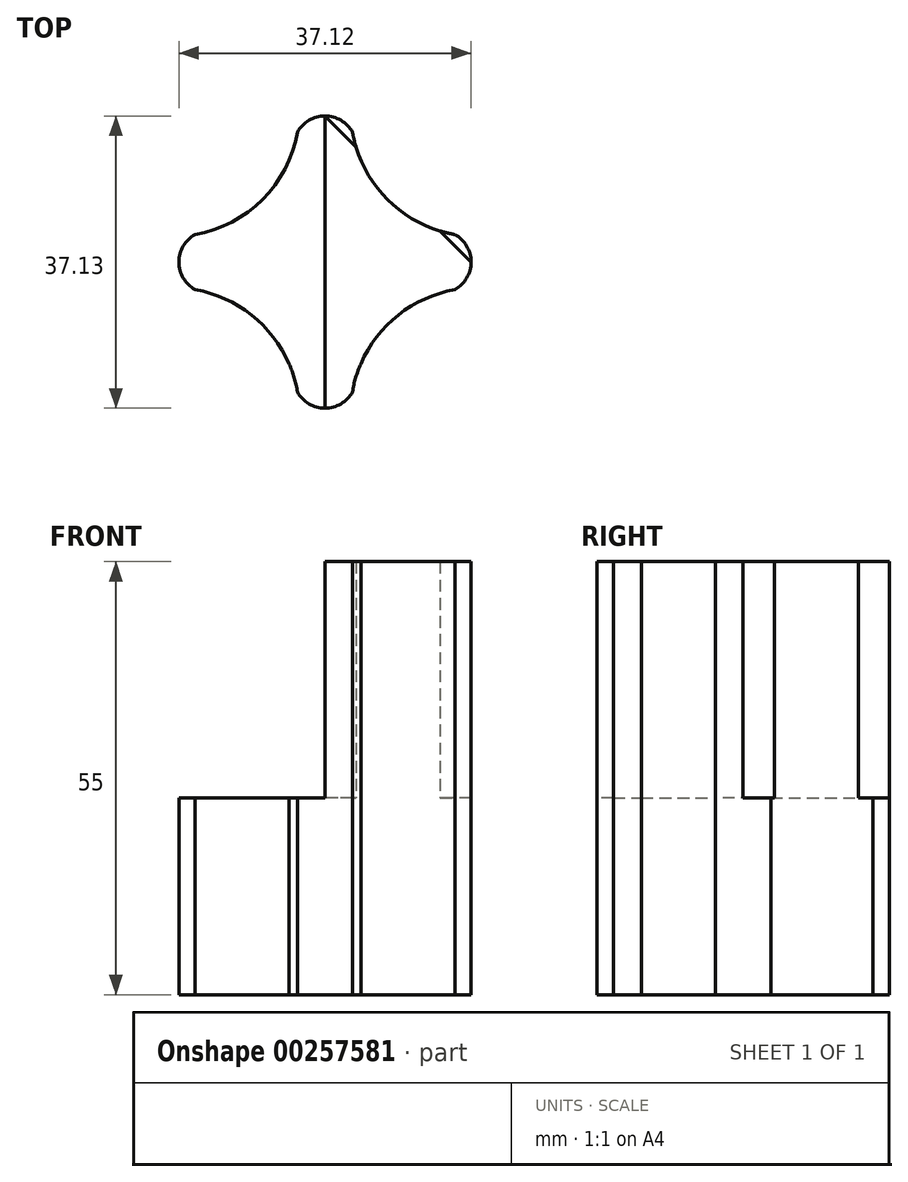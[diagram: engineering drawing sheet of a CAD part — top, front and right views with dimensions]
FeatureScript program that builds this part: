
annotation { "Feature Type Name" : "Feature", "Feature Type Description" : "" }
export const myFeature = defineFeature(function(context is Context, id is Id, definition is map)
    precondition{}
    {
        {
            var Q0;
            Q0=qCreatedBy(makeId("Top.planeOp"),FACE);
            var sketch = newSketch(context, id + "F0", { "sketchPlane" : qUnion([Q0])});
            skPoint(sketch, "E0", {"position": v(0.76, 10.62) * mm});
            skPoint(sketch, "E1", {"position": v(17.26, -5.88) * mm});
            skArc(sketch, "E2", {"start": v(4.26, 10.62) * mm, "mid": v(8.7, 2.06) * mm, "end": v(17.26, -2.38) * mm});
            skArc(sketch, "E3.MirrorCS", {"start": v(4.26, -22.38) * mm, "mid": v(8.7, -13.83) * mm, "end": v(17.26, -9.38) * mm});
            skArc(sketch, "E4.MirrorCS", {"start": v(-2.74, 10.62) * mm, "mid": v(-7.19, 2.06) * mm, "end": v(-15.74, -2.38) * mm});
            skArc(sketch, "E5.MirrorCS", {"start": v(-2.74, -22.38) * mm, "mid": v(-7.19, -13.83) * mm, "end": v(-15.74, -9.38) * mm});
            skArc(sketch, "E6", {"start": v(4.26, 10.62) * mm, "mid": v(0.76, 12.68) * mm, "end": v(-2.74, 10.62) * mm});
            skArc(sketch, "E7.MirrorCS", {"start": v(4.26, -22.38) * mm, "mid": v(0.76, -24.45) * mm, "end": v(-2.74, -22.38) * mm});
            skArc(sketch, "E8", {"start": v(17.26, -9.38) * mm, "mid": v(19.32, -5.88) * mm, "end": v(17.26, -2.38) * mm});
            skArc(sketch, "E9.MirrorCS", {"start": v(-15.74, -9.38) * mm, "mid": v(-17.8, -5.88) * mm, "end": v(-15.74, -2.38) * mm});
            skArc(sketch, "E10", {"start": v(-8.77, 16.95) * mm, "mid": v(0.83, 12.68) * mm, "end": v(10.38, 17.05) * mm});
            skArc(sketch, "E11.1.0", {"start": v(-20.21, -5.21) * mm, "mid": v(-13.18, 2.6) * mm, "end": v(-14.4, 13.04) * mm});
            skArc(sketch, "E11.2.0", {"start": v(-2.67, -22.94) * mm, "mid": v(-7.93, -13.84) * mm, "end": v(-18.23, -11.77) * mm});
            skArc(sketch, "E11.3.0", {"start": v(19.61, -11.74) * mm, "mid": v(9.34, -13.92) * mm, "end": v(4.18, -23.08) * mm});
            skArc(sketch, "E11.4.0", {"start": v(15.84, 12.92) * mm, "mid": v(14.75, 2.47) * mm, "end": v(21.86, -5.26) * mm});
            skPoint(sketch, "E11.center", {"position": v(0.76, -2) * mm});
            skArc(sketch, "E12", {"start": v(-2.67, -22.94) * mm, "mid": v(0.72, -24.94) * mm, "end": v(4.18, -23.08) * mm});
            skArc(sketch, "E13.1.0", {"start": v(-20.21, -5.21) * mm, "mid": v(-21.07, -9.05) * mm, "end": v(-18.23, -11.77) * mm});
            skArc(sketch, "E13.2.0", {"start": v(-8.77, 16.95) * mm, "mid": v(-12.69, 16.58) * mm, "end": v(-14.4, 13.04) * mm});
            skArc(sketch, "E13.3.0", {"start": v(15.84, 12.92) * mm, "mid": v(14.28, 16.53) * mm, "end": v(10.38, 17.05) * mm});
            skArc(sketch, "E13.4.0", {"start": v(19.61, -11.74) * mm, "mid": v(22.57, -9.14) * mm, "end": v(21.86, -5.26) * mm});
            skLineSegment(sketch, "E13.anchor1", {"start": v(0.76, -2) * mm, "end": v(-2.67, -22.94) * mm, "construction": true});
            skLineSegment(sketch, "E13.anchor2", {"start": v(0.76, -2) * mm, "end": v(19.61, -11.74) * mm, "construction": true});
            skSolve(sketch);
        }
        {
            var Q0;
            {var subQ9=sQuery(id+"F0.wireOp",EDGE,"E2");Q0=makeQuery(id+"F0.imprint","IMPRINT",FACE,{"disambiguationData":[TD([[makeQuery(id+"F0.imprint","IMPRINT",EDGE,{"derivedFrom":subQ9}),-1.0]])]});}
            extrude(context, id + "F1", {"entities" : qUnion([Q0]), "depth" : 25 * mm});
        }
        {
            var Q0;
            Q0=makeQuery(id+"F1.opExtrude","CAP_FACE",FACE,{"disambiguationData":[OSD([sQuery(id+"F0.wireOp",EDGE,"E2"),sQuery(id+"F0.wireOp",EDGE,"E3.MirrorCS"),sQuery(id+"F0.wireOp",EDGE,"E4.MirrorCS"),sQuery(id+"F0.wireOp",EDGE,"E5.MirrorCS"),sQuery(id+"F0.wireOp",EDGE,"E6"),sQuery(id+"F0.wireOp",EDGE,"E7.MirrorCS"),sQuery(id+"F0.wireOp",EDGE,"E8"),sQuery(id+"F0.wireOp",EDGE,"E9.MirrorCS"),sQuery(id+"F0.wireOp",EDGE,"E11.2.0"),sQuery(id+"F0.wireOp",EDGE,"E11.3.0")])],"isStart":false});
            var sketch = newSketch(context, id + "F2", { "sketchPlane" : qUnion([Q0])});
            skLineSegment(sketch, "E14", {"start": v(-17.8, -5.88) * mm, "end": v(19.32, -5.88) * mm});
            skLineSegment(sketch, "E15", {"start": v(19.32, -5.88) * mm, "end": v(0.76, 12.68) * mm});
            skLineSegment(sketch, "E16", {"start": v(0.76, 12.68) * mm, "end": v(0.76, -24.45) * mm});
            skPoint(sketch, "E17", {"position": v(0.76, -5.88) * mm});
            skCircle(sketch, "E18", {"center": v(0.76, -5.88) * mm, "radius": 5 * mm});
            skSolve(sketch);
        }
        {
            var Q0;
            {var subQ0=sQuery(id+"F2.wireOp",EDGE,"E18");var subQ1=sQuery(id+"F2.wireOp",EDGE,"E14");var subQ2=makeQuery(id+"F2.imprint","INTERSECT",VERTEX,{"disambiguationData":[OD(0.0)],"derivedFrom":[subQ1,subQ0]});Q0=makeQuery(id+"F2.imprint","IMPRINT",FACE,{"disambiguationData":[TD([[makeQuery(id+"F2.imprint","IMPRINT",EDGE,{"disambiguationData":[TD([[subQ2,-1.0]])],"derivedFrom":subQ1}),1.0]])]});}
            var Q1;
            {var subQ0=sQuery(id+"F2.wireOp",EDGE,"E18");var subQ1=sQuery(id+"F2.wireOp",EDGE,"E14");var subQ2=makeQuery(id+"F2.imprint","INTERSECT",VERTEX,{"disambiguationData":[OD(0.0)],"derivedFrom":[subQ1,subQ0]});Q1=makeQuery(id+"F2.imprint","IMPRINT",FACE,{"disambiguationData":[TD([[makeQuery(id+"F2.imprint","IMPRINT",EDGE,{"disambiguationData":[TD([[subQ2,-1.0]])],"derivedFrom":subQ1}),-1.0]])]});}
            var Q2;
            {var subQ0=sQuery(id+"F2.wireOp",EDGE,"E16");var subQ1=sQuery(id+"F2.wireOp",EDGE,"E14");var subQ2=makeQuery(id+"F2.imprint","INTERSECT",VERTEX,{"derivedFrom":[subQ1,subQ0]});Q2=makeQuery(id+"F2.imprint","IMPRINT",FACE,{"disambiguationData":[TD([[makeQuery(id+"F2.imprint","IMPRINT",EDGE,{"disambiguationData":[TD([[subQ2,-1.0]])],"derivedFrom":subQ1}),1.0]])]});}
            var Q3;
            {var subQ0=sQuery(id+"F2.wireOp",EDGE,"E16");var subQ1=sQuery(id+"F2.wireOp",EDGE,"E14");var subQ2=makeQuery(id+"F2.imprint","INTERSECT",VERTEX,{"derivedFrom":[subQ1,subQ0]});Q3=makeQuery(id+"F2.imprint","IMPRINT",FACE,{"disambiguationData":[TD([[makeQuery(id+"F2.imprint","IMPRINT",EDGE,{"disambiguationData":[TD([[subQ2,-1.0]])],"derivedFrom":subQ1}),-1.0]])]});}
            extrude(context, id + "F3", {"entities" : qUnion([Q0, Q1, Q2, Q3]), "operationType" : NewBodyOperationType.ADD, "depth" : 30 * mm});
        }
    });
